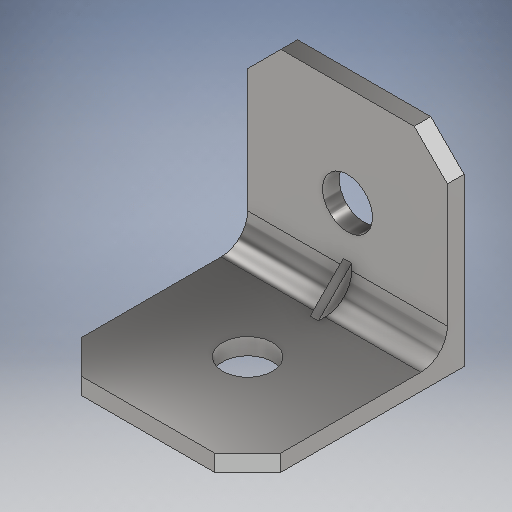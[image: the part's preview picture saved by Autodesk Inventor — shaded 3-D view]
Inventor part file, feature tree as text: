
AUTODESK INVENTOR PART (.ipt)
format: ipt  version: 2025.2 (Build 292293000, 293)  size: 319,488 bytes
history: native  units: mm
features: extrude x5, sketch x5, chamfer x2, plane x1
ambient origin geometry x8: Origin, YZ Plane, XZ Plane, XY Plane, X Axis, Y Axis, Z Axis, Center Point
bodies: Solid1 (feature_tree)
feature tree (13):
  extrude  "BOTTOM"  Depth=76.2mm
  extrude  "SIDE"  TaperAngle=0.0deg  [1 undecoded]
  extrude  "HOLE BOTT"  Depth=76.2mm
  extrude  "HOLE SIDE"  TaperAngle=0.0deg  [1 undecoded]
  chamfer  "CHM TOP"  Distance=38.1mm
  plane  "Work Plane1"
  extrude  "BRACE"  Depth=3.175mm
  chamfer  "CHM BOTT"  Distance=6.35mm
  sketch  "Sketch1"  dims[d0=76.2mm d1=76.2mm]
  sketch  "Sketch2"  dims[d2=6.35mm d3=0.0mm]
  sketch  "Sketch3"  dims[d4=76.2mm d5=76.2mm]
  sketch  "Sketch4"  dims[d6=6.35mm d7=0.0mm]
  sketch  "Sketch6"  dims[d9=19.05mm d10=38.1mm d11=38.1mm d12=6.35mm d13=0.0mm d14=19.05mm d15=38.1mm d16=38.1mm d17=6.35mm d18=0.0mm d19=12.7mm d20=3.175mm d21=45.0deg d24=-38.1mm d25=12.7mm d27=12.7mm d28=3.175mm d29=0.0mm d30=10.16mm d31=12.7mm d32=3.175mm d33=45.0deg]
note: 2 required parameter values undecoded (feature->parameter linkage not recoverable at this tier; creation-order binding heuristic only, values carry confidence <= 0.55)
